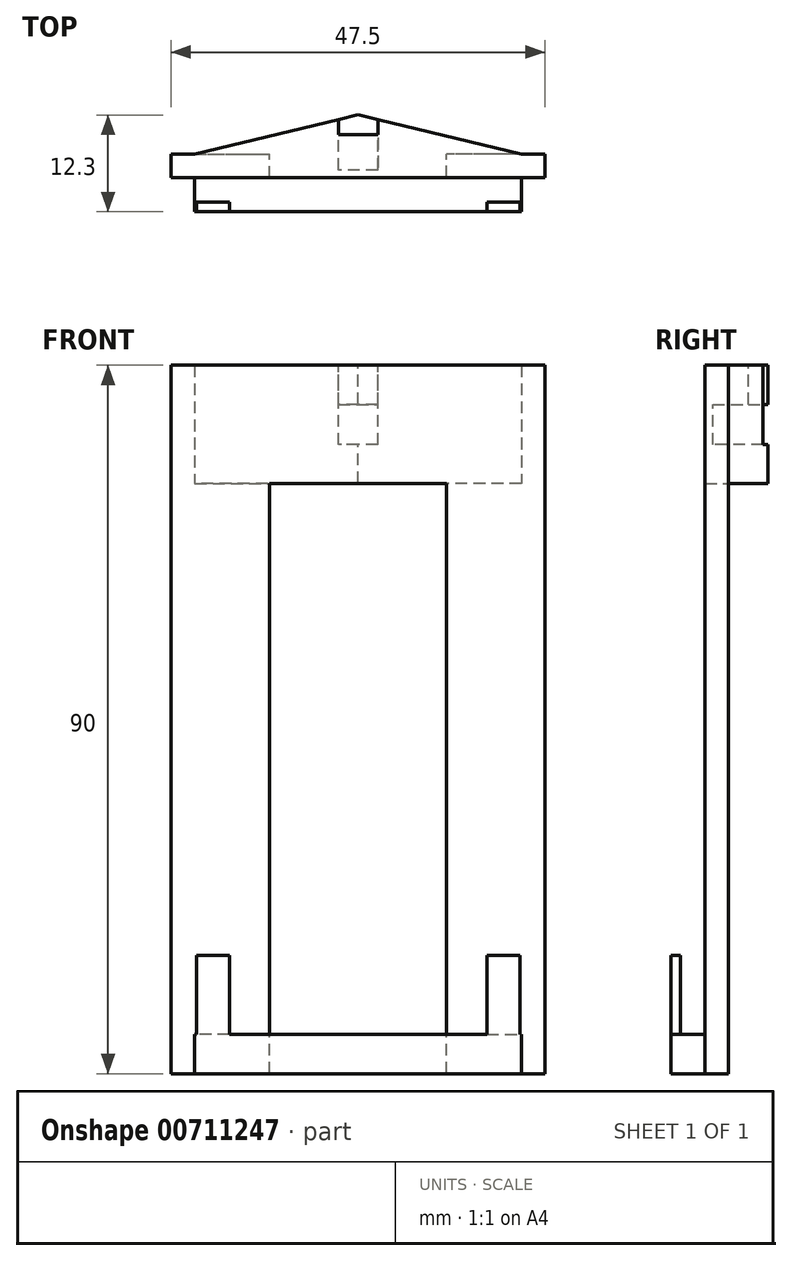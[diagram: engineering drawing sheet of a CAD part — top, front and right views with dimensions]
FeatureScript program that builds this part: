
annotation { "Feature Type Name" : "Feature", "Feature Type Description" : "" }
export const myFeature = defineFeature(function(context is Context, id is Id, definition is map)
    precondition{}
    {
        {
            var Q0;
            Q0=qCreatedBy(makeId("Top.planeOp"),FACE);
            var sketch = newSketch(context, id + "F0", { "sketchPlane" : qUnion([Q0])});
            skLineSegment(sketch, "E0.bottom", {"start": v(-89.05, 1.71) * mm, "end": v(-84.85, 1.71) * mm});
            skLineSegment(sketch, "E0.top", {"start": v(-89.05, 0.51) * mm, "end": v(-84.85, 0.51) * mm});
            skLineSegment(sketch, "E0.left", {"start": v(-89.05, 1.71) * mm, "end": v(-89.05, 0.51) * mm});
            skLineSegment(sketch, "E0.right", {"start": v(-84.85, 1.71) * mm, "end": v(-84.85, 0.51) * mm});
            skLineSegment(sketch, "E1.bottom", {"start": v(-52.15, 1.71) * mm, "end": v(-47.95, 1.71) * mm});
            skLineSegment(sketch, "E1.top", {"start": v(-52.15, 0.51) * mm, "end": v(-47.95, 0.51) * mm});
            skLineSegment(sketch, "E1.left", {"start": v(-52.15, 1.71) * mm, "end": v(-52.15, 0.51) * mm});
            skLineSegment(sketch, "E1.right", {"start": v(-47.95, 1.71) * mm, "end": v(-47.95, 0.51) * mm});
            skLineSegment(sketch, "E2.bottom", {"start": v(-89.05, 1.71) * mm, "end": v(-47.95, 1.71) * mm});
            skLineSegment(sketch, "E2.top", {"start": v(-89.05, 0.51) * mm, "end": v(-47.95, 0.51) * mm});
            skSolve(sketch);
        }
        {
            var Q0;
            {var subQ0=sQuery(id+"F0.wireOp",EDGE,"E0.right");Q0=makeQuery(id+"F0.imprint","IMPRINT",FACE,{"disambiguationData":[TD([[makeQuery(id+"F0.imprint","IMPRINT",EDGE,{"derivedFrom":subQ0}),-1.0]])]});}
            var Q1;
            {var subQ0=sQuery(id+"F0.wireOp",EDGE,"E1.left");Q1=makeQuery(id+"F0.imprint","IMPRINT",FACE,{"disambiguationData":[TD([[makeQuery(id+"F0.imprint","IMPRINT",EDGE,{"derivedFrom":subQ0}),1.0]])]});}
            extrude(context, id + "F1", {"entities" : qUnion([Q0, Q1]), "depth" : 15 * mm, "offsetDistance" : 25 * mm});
        }
        {
            var Q0;
            {var subQ0=sQuery(id+"F0.wireOp",EDGE,"E0.right");Q0=makeQuery(id+"F0.imprint","IMPRINT",FACE,{"disambiguationData":[TD([[makeQuery(id+"F0.imprint","IMPRINT",EDGE,{"derivedFrom":subQ0}),1.0]])]});}
            extrude(context, id + "F2", {"entities" : qUnion([Q0]), "depth" : 5 * mm, "offsetDistance" : 25 * mm});
        }
        {
            var Q0;
            Q0=makeQuery(id+"F2.opExtrude","CAP_FACE",FACE,{"disambiguationData":[OSD([sQuery(id+"F0.wireOp",EDGE,"E0.right"),sQuery(id+"F0.wireOp",EDGE,"E1.left"),sQuery(id+"F0.wireOp",EDGE,"E2.bottom"),sQuery(id+"F0.wireOp",EDGE,"E2.top")])],"isStart":true});
            var sketch = newSketch(context, id + "F3", { "sketchPlane" : qUnion([Q0])});
            skLineSegment(sketch, "E3", {"start": v(-84.85, -0.51) * mm, "end": v(-89.25, -0.51) * mm});
            skLineSegment(sketch, "E4", {"start": v(-89.25, -0.51) * mm, "end": v(-89.25, -4.81) * mm});
            skLineSegment(sketch, "E5", {"start": v(-84.85, -0.51) * mm, "end": v(-52.15, -0.51) * mm});
            skLineSegment(sketch, "E6", {"start": v(-52.15, -0.51) * mm, "end": v(-47.75, -0.51) * mm});
            skLineSegment(sketch, "E7", {"start": v(-47.75, -0.51) * mm, "end": v(-47.75, -4.81) * mm});
            skLineSegment(sketch, "E8", {"start": v(-89.25, -4.81) * mm, "end": v(-68.5, -4.86) * mm});
            skPoint(sketch, "E8.endSnap0", {"position": v(-68.5, -1.71) * mm});
            skLineSegment(sketch, "E9", {"start": v(-68.5, -4.86) * mm, "end": v(-47.75, -4.81) * mm});
            skSolve(sketch);
        }
        {
            var Q0;
            Q0 = qSketchRegion(id + "F3", true);
            extrude(context, id + "F4", {"entities" : qUnion([Q0]), "oppositeDirection" : true, "depth" : 5 * mm, "offsetDistance" : 25 * mm});
        }
        {
            var Q0;
            Q0=makeQuery(id+"F1.opExtrude","SWEPT_BODY",BODY,{"disambiguationData":[OSD([sQuery(id+"F0.wireOp",EDGE,"E0.right"),sQuery(id+"F0.wireOp",EDGE,"E2.bottom"),sQuery(id+"F0.wireOp",EDGE,"E2.top"),sQuery(id+"F0.wireOp",EDGE,"E0.left")])]});
            var Q1;
            Q1=makeQuery(id+"F1.opExtrude","SWEPT_BODY",BODY,{"disambiguationData":[OSD([sQuery(id+"F0.wireOp",EDGE,"E1.left"),sQuery(id+"F0.wireOp",EDGE,"E2.bottom"),sQuery(id+"F0.wireOp",EDGE,"E2.top"),sQuery(id+"F0.wireOp",EDGE,"E1.right")])]});
            var Q2;
            Q2=makeQuery(id+"F2.opExtrude","SWEPT_BODY",BODY,{"disambiguationData":[OSD([sQuery(id+"F0.wireOp",EDGE,"E0.right"),sQuery(id+"F0.wireOp",EDGE,"E1.left"),sQuery(id+"F0.wireOp",EDGE,"E2.bottom"),sQuery(id+"F0.wireOp",EDGE,"E2.top")])]});
            var Q3;
            Q3=makeQuery(id+"F4.opExtrude","SWEPT_BODY",BODY,{"disambiguationData":[OSD([sQuery(id+"F3.wireOp",EDGE,"E3"),sQuery(id+"F3.wireOp",EDGE,"E4"),sQuery(id+"F3.wireOp",EDGE,"E5"),sQuery(id+"F3.wireOp",EDGE,"E6"),sQuery(id+"F3.wireOp",EDGE,"E7"),sQuery(id+"F3.wireOp",EDGE,"E8"),sQuery(id+"F3.wireOp",EDGE,"E9")])]});
            booleanBodies(context, id + "F5", {"operationType" : BooleanOperationType.UNION, "tools" : qUnion([Q0, Q1, Q2, Q3])});
        }
        {
            var Q0;
            Q0 = qSketchRegion(id + "F3", true);
            extrude(context, id + "F6", {"entities" : qUnion([Q0]), "operationType" : NewBodyOperationType.ADD, "oppositeDirection" : true, "depth" : 5 * mm, "offsetDistance" : 25 * mm});
        }
        {
            var Q0;
            {var subQ0=sQuery(id+"F0.wireOp",EDGE,"E2.top");var subQ1=sQuery(id+"F0.wireOp",EDGE,"E2.bottom");var subQ2=sQuery(id+"F0.wireOp",EDGE,"E1.left");var subQ3=sQuery(id+"F0.wireOp",EDGE,"E0.right");Q0=makeQuery(id+"F5.opBoolean","MERGE",FACE,{"derivedFrom":[makeQuery(id+"F1.opExtrude","CAP_FACE",FACE,{"disambiguationData":[OSD([subQ3,subQ1,subQ0,sQuery(id+"F0.wireOp",EDGE,"E0.left")])],"isStart":true}),makeQuery(id+"F1.opExtrude","CAP_FACE",FACE,{"disambiguationData":[OSD([subQ2,subQ1,subQ0,sQuery(id+"F0.wireOp",EDGE,"E1.right")])],"isStart":true}),makeQuery(id+"F2.opExtrude","CAP_FACE",FACE,{"disambiguationData":[OSD([subQ3,subQ2,subQ1,subQ0])],"isStart":true}),makeQuery(id+"F4.opExtrude","CAP_FACE",FACE,{"disambiguationData":[OSD([sQuery(id+"F3.wireOp",EDGE,"E3"),sQuery(id+"F3.wireOp",EDGE,"E4"),sQuery(id+"F3.wireOp",EDGE,"E5"),sQuery(id+"F3.wireOp",EDGE,"E6"),sQuery(id+"F3.wireOp",EDGE,"E7"),sQuery(id+"F3.wireOp",EDGE,"E8"),sQuery(id+"F3.wireOp",EDGE,"E9")])],"isStart":true})]});}
            var sketch = newSketch(context, id + "F7", { "sketchPlane" : qUnion([Q0])});
            skLineSegment(sketch, "E10.bottom", {"start": v(-89.25, -4.81) * mm, "end": v(-79.75, -4.81) * mm});
            skLineSegment(sketch, "E10.top", {"start": v(-89.25, -7.81) * mm, "end": v(-79.75, -7.81) * mm});
            skLineSegment(sketch, "E10.left", {"start": v(-89.25, -4.81) * mm, "end": v(-89.25, -7.81) * mm});
            skLineSegment(sketch, "E10.right", {"start": v(-79.75, -4.81) * mm, "end": v(-79.75, -7.81) * mm});
            skLineSegment(sketch, "E11.bottom", {"start": v(-47.75, -4.81) * mm, "end": v(-57.25, -4.81) * mm});
            skLineSegment(sketch, "E11.top", {"start": v(-47.75, -7.81) * mm, "end": v(-57.25, -7.81) * mm});
            skLineSegment(sketch, "E11.left", {"start": v(-47.75, -4.81) * mm, "end": v(-47.75, -7.81) * mm});
            skLineSegment(sketch, "E11.right", {"start": v(-57.25, -4.81) * mm, "end": v(-57.25, -7.81) * mm});
            skSolve(sketch);
        }
        {
            var Q0;
            Q0 = qSketchRegion(id + "F7", true);
            extrude(context, id + "F8", {"entities" : qUnion([Q0]), "operationType" : NewBodyOperationType.ADD, "oppositeDirection" : true, "depth" : 90 * mm, "offsetDistance" : 25 * mm});
        }
        {
            var Q0;
            Q0=makeQuery(id+"F8.opExtrude","CAP_FACE",FACE,{"disambiguationData":[OSD([sQuery(id+"F7.wireOp",EDGE,"E11.bottom"),sQuery(id+"F7.wireOp",EDGE,"E11.top"),sQuery(id+"F7.wireOp",EDGE,"E11.left"),sQuery(id+"F7.wireOp",EDGE,"E11.right")])],"isStart":false});
            var sketch = newSketch(context, id + "F9", { "sketchPlane" : qUnion([Q0])});
            skLineSegment(sketch, "E12.bottom", {"start": v(-47.75, 4.81) * mm, "end": v(-89.25, 4.81) * mm});
            skLineSegment(sketch, "E12.top", {"start": v(-47.75, 7.81) * mm, "end": v(-89.25, 7.81) * mm});
            skLineSegment(sketch, "E12.left", {"start": v(-47.75, 4.81) * mm, "end": v(-47.75, 7.81) * mm});
            skLineSegment(sketch, "E12.right", {"start": v(-89.25, 4.81) * mm, "end": v(-89.25, 7.81) * mm});
            skLineSegment(sketch, "E13", {"start": v(-68.5, 7.81) * mm, "end": v(-68.5, 12.81) * mm});
            skLineSegment(sketch, "E14", {"start": v(-47.75, 7.81) * mm, "end": v(-68.5, 12.81) * mm});
            skLineSegment(sketch, "E15", {"start": v(-68.5, 12.81) * mm, "end": v(-89.25, 7.81) * mm});
            skLineSegment(sketch, "E16", {"start": v(-68.5, 10.31) * mm, "end": v(-66, 10.31) * mm});
            skLineSegment(sketch, "E17", {"start": v(-68.5, 10.31) * mm, "end": v(-71, 10.31) * mm});
            skLineSegment(sketch, "E18", {"start": v(-71, 10.31) * mm, "end": v(-71, 105.31) * mm});
            skLineSegment(sketch, "E19", {"start": v(-71, 105.31) * mm, "end": v(-66, 105.31) * mm});
            skLineSegment(sketch, "E20", {"start": v(-66, 105.31) * mm, "end": v(-66, 10.31) * mm});
            skSolve(sketch);
        }
        {
            var Q0;
            {var subQ0=sQuery(id+"F9.wireOp",EDGE,"E12.right");Q0=makeQuery(id+"F9.imprint","IMPRINT",FACE,{"disambiguationData":[TD([[makeQuery(id+"F9.imprint","IMPRINT",EDGE,{"derivedFrom":subQ0}),-1.0]])]});}
            var Q1;
            {var subQ0=sQuery(id+"F9.wireOp",EDGE,"E12.left");Q1=makeQuery(id+"F9.imprint","IMPRINT",FACE,{"disambiguationData":[TD([[makeQuery(id+"F9.imprint","IMPRINT",EDGE,{"derivedFrom":subQ0}),1.0]])]});}
            var Q2;
            {var subQ8=sQuery(id+"F9.wireOp",EDGE,"E16");Q2=makeQuery(id+"F9.imprint","IMPRINT",FACE,{"disambiguationData":[TD([[makeQuery(id+"F9.imprint","IMPRINT",EDGE,{"derivedFrom":subQ8}),-1.0]])]});}
            var Q3;
            {var subQ7=sQuery(id+"F9.wireOp",EDGE,"E17");Q3=makeQuery(id+"F9.imprint","IMPRINT",FACE,{"disambiguationData":[TD([[makeQuery(id+"F9.imprint","IMPRINT",EDGE,{"derivedFrom":subQ7}),1.0]])]});}
            var Q4;
            {var subQ3=sQuery(id+"F9.wireOp",EDGE,"E17");Q4=makeQuery(id+"F9.imprint","IMPRINT",FACE,{"disambiguationData":[TD([[makeQuery(id+"F9.imprint","IMPRINT",EDGE,{"derivedFrom":subQ3}),-1.0]])]});}
            var Q5;
            {var subQ3=sQuery(id+"F9.wireOp",EDGE,"E16");Q5=makeQuery(id+"F9.imprint","IMPRINT",FACE,{"disambiguationData":[TD([[makeQuery(id+"F9.imprint","IMPRINT",EDGE,{"derivedFrom":subQ3}),1.0]])]});}
            extrude(context, id + "F10", {"entities" : qUnion([Q0, Q1, Q2, Q3, Q4, Q5]), "operationType" : NewBodyOperationType.ADD, "oppositeDirection" : true, "depth" : 15 * mm, "offsetDistance" : 25 * mm});
        }
        {
            var Q0;
            {var subQ3=sQuery(id+"F9.wireOp",EDGE,"E17");Q0=makeQuery(id+"F9.imprint","IMPRINT",FACE,{"disambiguationData":[TD([[makeQuery(id+"F9.imprint","IMPRINT",EDGE,{"derivedFrom":subQ3}),-1.0]])]});}
            var Q1;
            {var subQ3=sQuery(id+"F9.wireOp",EDGE,"E16");Q1=makeQuery(id+"F9.imprint","IMPRINT",FACE,{"disambiguationData":[TD([[makeQuery(id+"F9.imprint","IMPRINT",EDGE,{"derivedFrom":subQ3}),1.0]])]});}
            extrude(context, id + "F11", {"entities" : qUnion([Q0, Q1]), "operationType" : NewBodyOperationType.REMOVE, "oppositeDirection" : true, "depth" : 10.1 * mm, "offsetDistance" : 25 * mm});
        }
        {
            var Q0;
            {var subQ3=sQuery(id+"F9.wireOp",EDGE,"E16");Q0=makeQuery(id+"F9.imprint","IMPRINT",FACE,{"disambiguationData":[TD([[makeQuery(id+"F9.imprint","IMPRINT",EDGE,{"derivedFrom":subQ3}),1.0]])]});}
            var Q1;
            {var subQ3=sQuery(id+"F9.wireOp",EDGE,"E17");Q1=makeQuery(id+"F9.imprint","IMPRINT",FACE,{"disambiguationData":[TD([[makeQuery(id+"F9.imprint","IMPRINT",EDGE,{"derivedFrom":subQ3}),-1.0]])]});}
            extrude(context, id + "F12", {"entities" : qUnion([Q0, Q1]), "oppositeDirection" : true, "depth" : 5 * mm, "offsetDistance" : 25 * mm});
        }
        {
            var Q0;
            Q0=makeQuery(id+"F11.boolean.opBoolean","COPY",FACE,{"derivedFrom":makeQuery(id+"F11.opExtrude","SWEPT_FACE",FACE,{"disambiguationData":[OSD([sQuery(id+"F9.wireOp",EDGE,"E16"),sQuery(id+"F9.wireOp",EDGE,"E17")])]})});
            var sketch = newSketch(context, id + "F13", { "sketchPlane" : qUnion([Q0])});
            skLineSegment(sketch, "E21.bottom", {"start": v(71, 85) * mm, "end": v(66, 85) * mm});
            skLineSegment(sketch, "E21.top", {"start": v(71, 79.9) * mm, "end": v(66, 79.9) * mm});
            skLineSegment(sketch, "E21.left", {"start": v(71, 85) * mm, "end": v(71, 79.9) * mm});
            skLineSegment(sketch, "E21.right", {"start": v(66, 85) * mm, "end": v(66, 79.9) * mm});
            skSolve(sketch);
        }
        {
            var Q0;
            Q0 = qSketchRegion(id + "F13", true);
            extrude(context, id + "F14", {"entities" : qUnion([Q0]), "operationType" : NewBodyOperationType.REMOVE, "oppositeDirection" : true, "depth" : 4.5 * mm, "offsetDistance" : 25 * mm});
        }
        {
            var Q0;
            {var subQ0=sQuery(id+"F0.wireOp",EDGE,"E2.top");var subQ1=sQuery(id+"F0.wireOp",EDGE,"E2.bottom");var subQ2=sQuery(id+"F0.wireOp",EDGE,"E1.left");var subQ3=sQuery(id+"F0.wireOp",EDGE,"E0.right");Q0=makeQuery(id+"F8.boolean.opBoolean","MERGE",FACE,{"derivedFrom":[makeQuery(id+"F5.opBoolean","MERGE",FACE,{"derivedFrom":[makeQuery(id+"F1.opExtrude","CAP_FACE",FACE,{"disambiguationData":[OSD([subQ3,subQ1,subQ0,sQuery(id+"F0.wireOp",EDGE,"E0.left")])],"isStart":true}),makeQuery(id+"F1.opExtrude","CAP_FACE",FACE,{"disambiguationData":[OSD([subQ2,subQ1,subQ0,sQuery(id+"F0.wireOp",EDGE,"E1.right")])],"isStart":true}),makeQuery(id+"F2.opExtrude","CAP_FACE",FACE,{"disambiguationData":[OSD([subQ3,subQ2,subQ1,subQ0])],"isStart":true}),makeQuery(id+"F4.opExtrude","CAP_FACE",FACE,{"disambiguationData":[OSD([sQuery(id+"F3.wireOp",EDGE,"E3"),sQuery(id+"F3.wireOp",EDGE,"E4"),sQuery(id+"F3.wireOp",EDGE,"E5"),sQuery(id+"F3.wireOp",EDGE,"E6"),sQuery(id+"F3.wireOp",EDGE,"E7"),sQuery(id+"F3.wireOp",EDGE,"E8"),sQuery(id+"F3.wireOp",EDGE,"E9")])],"isStart":true})]}),makeQuery(id+"F8.opExtrude","CAP_FACE",FACE,{"disambiguationData":[OSD([sQuery(id+"F7.wireOp",EDGE,"E10.bottom"),sQuery(id+"F7.wireOp",EDGE,"E10.top"),sQuery(id+"F7.wireOp",EDGE,"E10.left"),sQuery(id+"F7.wireOp",EDGE,"E10.right")])],"isStart":true}),makeQuery(id+"F8.opExtrude","CAP_FACE",FACE,{"disambiguationData":[OSD([sQuery(id+"F7.wireOp",EDGE,"E11.bottom"),sQuery(id+"F7.wireOp",EDGE,"E11.top"),sQuery(id+"F7.wireOp",EDGE,"E11.left"),sQuery(id+"F7.wireOp",EDGE,"E11.right")])],"isStart":true})]});}
            var sketch = newSketch(context, id + "F15", { "sketchPlane" : qUnion([Q0])});
            skLineSegment(sketch, "E22.bottom", {"start": v(-47.75, -7.81) * mm, "end": v(-44.75, -7.81) * mm});
            skLineSegment(sketch, "E22.top", {"start": v(-47.75, -4.81) * mm, "end": v(-44.75, -4.81) * mm});
            skLineSegment(sketch, "E22.left", {"start": v(-47.75, -7.81) * mm, "end": v(-47.75, -4.81) * mm});
            skLineSegment(sketch, "E22.right", {"start": v(-44.75, -7.81) * mm, "end": v(-44.75, -4.81) * mm});
            skLineSegment(sketch, "E23.bottom", {"start": v(-89.25, -7.81) * mm, "end": v(-92.25, -7.81) * mm});
            skLineSegment(sketch, "E23.top", {"start": v(-89.25, -4.81) * mm, "end": v(-92.25, -4.81) * mm});
            skLineSegment(sketch, "E23.left", {"start": v(-89.25, -7.81) * mm, "end": v(-89.25, -4.81) * mm});
            skLineSegment(sketch, "E23.right", {"start": v(-92.25, -7.81) * mm, "end": v(-92.25, -4.81) * mm});
            skSolve(sketch);
        }
        {
            var Q0;
            Q0 = qSketchRegion(id + "F15", true);
            extrude(context, id + "F16", {"entities" : qUnion([Q0]), "operationType" : NewBodyOperationType.ADD, "oppositeDirection" : true, "depth" : 90 * mm, "offsetDistance" : 25 * mm});
        }
    });
